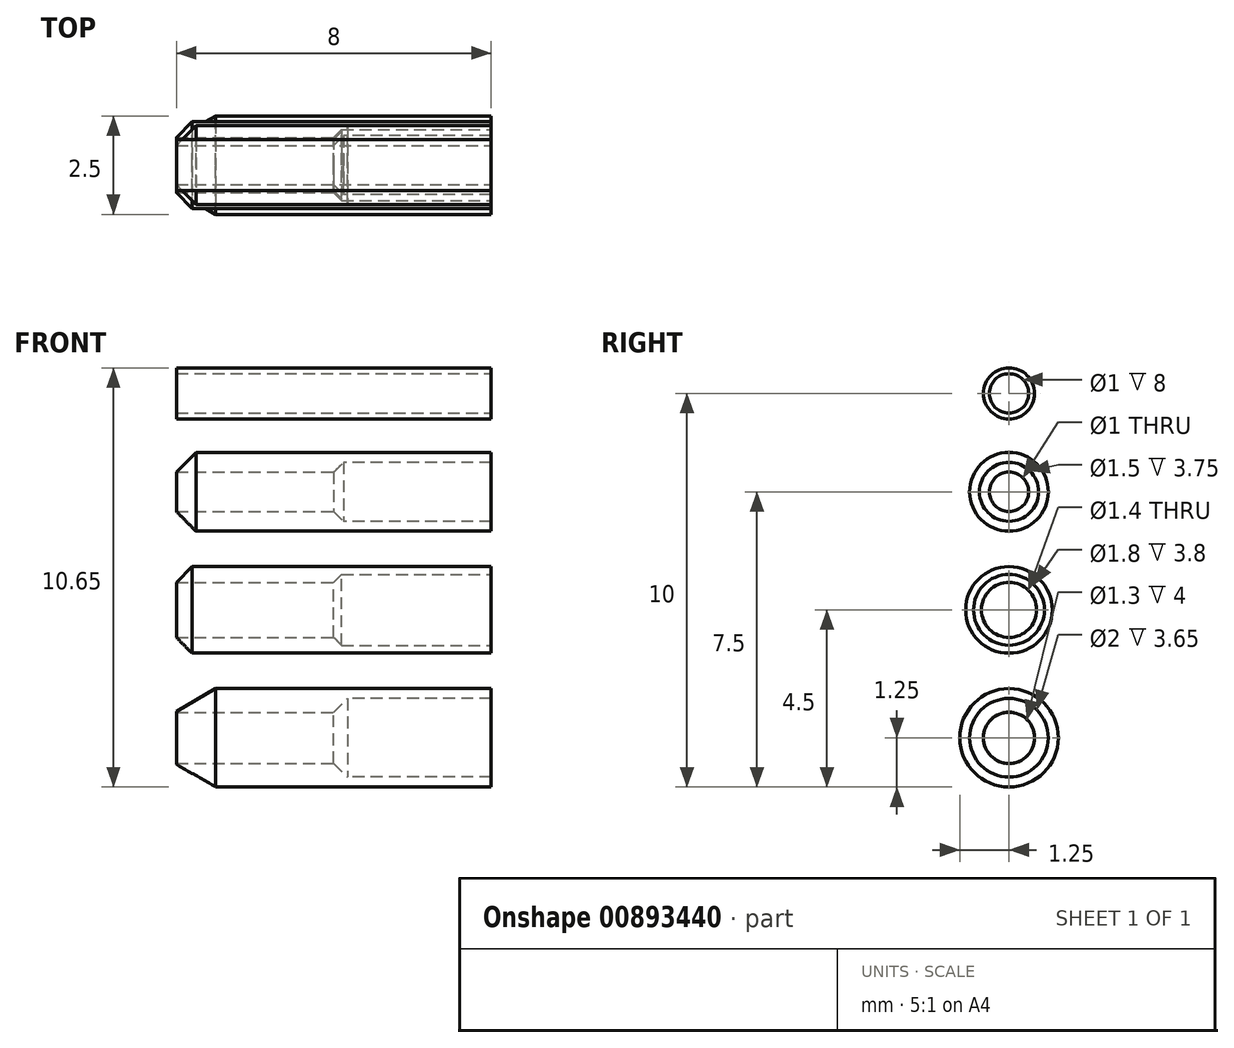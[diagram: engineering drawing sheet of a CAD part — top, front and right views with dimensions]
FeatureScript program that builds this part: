
annotation { "Feature Type Name" : "Feature", "Feature Type Description" : "" }
export const myFeature = defineFeature(function(context is Context, id is Id, definition is map)
    precondition{}
    {
        {
            var Q0;
            Q0=qCreatedBy(makeId("Right.planeOp"),FACE);
            var sketch = newSketch(context, id + "F0", { "sketchPlane" : qUnion([Q0])});
            skCircle(sketch, "E0", {"center": v(0, 0) * mm, "radius": 1.1 * mm});
            skCircle(sketch, "E1", {"center": v(0, 3) * mm, "radius": 1 * mm});
            skCircle(sketch, "E2", {"center": v(0, -3.25) * mm, "radius": 1.25 * mm});
            skCircle(sketch, "E3", {"center": v(0, 5.5) * mm, "radius": 0.65 * mm});
            skSolve(sketch);
        }
        {
            var Q0;
            Q0 = qSketchRegion(id + "F0", true);
            extrude(context, id + "F1", {"entities" : qUnion([Q0]), "endBound" : BoundingType.SYMMETRIC, "depth" : 8 * mm, "offsetDistance" : 25 * mm});
        }
        {
            var Q0;
            Q0=makeQuery(id+"F1.opExtrude","CAP_FACE",FACE,{"disambiguationData":[OSD([sQuery(id+"F0.wireOp",EDGE,"E1")])],"isStart":false});
            var sketch = newSketch(context, id + "F2", { "sketchPlane" : qUnion([Q0])});
            skPoint(sketch, "E4", {"position": v(0, 0) * mm});
            skPoint(sketch, "E5", {"position": v(0, 3) * mm});
            skPoint(sketch, "E6", {"position": v(0, 5.5) * mm});
            skPoint(sketch, "E7", {"position": v(0, -3.25) * mm});
            skSolve(sketch);
        }
        {
            var Q0;
            Q0=sQuery(id+"F2.wireOp",VERTEX,"E6");
            var Q1;
            Q1=makeQuery(id+"F1.opExtrude","SWEPT_BODY",BODY,{"disambiguationData":[OSD([sQuery(id+"F0.wireOp",EDGE,"E3")])]});
            hole(context, id + "F3", {"style" : HoleStyle.SIMPLE, "endStyle" : HoleEndStyle.THROUGH, "holeDiameter" : 1 * mm, "majorDiameter" : 5 * mm, "isTappedThrough" : true, "tappedDepth" : 12 * mm, "tapClearance" : 3, "locations" : qUnion([Q0]), "scope" : qUnion([Q1])});
        }
        {
            var Q0;
            Q0=sQuery(id+"F2.wireOp",VERTEX,"E7");
            var Q1;
            Q1=makeQuery(id+"F1.opExtrude","SWEPT_BODY",BODY,{"disambiguationData":[OSD([sQuery(id+"F0.wireOp",EDGE,"E2")])]});
            hole(context, id + "F4", {"style" : HoleStyle.SIMPLE, "endStyle" : HoleEndStyle.THROUGH, "holeDiameter" : 1.3 * mm, "majorDiameter" : 5 * mm, "isTappedThrough" : true, "tappedDepth" : 12 * mm, "tapClearance" : 3, "locations" : qUnion([Q0]), "scope" : qUnion([Q1])});
        }
        {
            var Q0;
            Q0=sQuery(id+"F2.wireOp",VERTEX,"E4");
            var Q1;
            Q1=makeQuery(id+"F1.opExtrude","SWEPT_BODY",BODY,{"disambiguationData":[OSD([sQuery(id+"F0.wireOp",EDGE,"E0")])]});
            hole(context, id + "F5", {"style" : HoleStyle.SIMPLE, "endStyle" : HoleEndStyle.THROUGH, "holeDiameter" : 1.4 * mm, "majorDiameter" : 5 * mm, "isTappedThrough" : true, "tappedDepth" : 12 * mm, "tapClearance" : 3, "locations" : qUnion([Q0]), "scope" : qUnion([Q1])});
        }
        {
            var Q0;
            Q0=sQuery(id+"F2.wireOp",VERTEX,"E5");
            var Q1;
            Q1=makeQuery(id+"F1.opExtrude","SWEPT_BODY",BODY,{"disambiguationData":[OSD([sQuery(id+"F0.wireOp",EDGE,"E1")])]});
            hole(context, id + "F6", {"style" : HoleStyle.SIMPLE, "endStyle" : HoleEndStyle.THROUGH, "holeDiameter" : 1 * mm, "majorDiameter" : 5 * mm, "isTappedThrough" : true, "tappedDepth" : 12 * mm, "tapClearance" : 3, "locations" : qUnion([Q0]), "scope" : qUnion([Q1])});
        }
        {
            var Q0;
            Q0=makeQuery(id+"F1.opExtrude","CAP_EDGE",EDGE,{"disambiguationData":[OSD([sQuery(id+"F0.wireOp",EDGE,"E0")])],"isStart":true});
            chamfer(context, id + "F7", {"entities" : qUnion([Q0]), "chamferType" : ChamferType.OFFSET_ANGLE, "width" : .4 * mm, "oppositeDirection" : false, "angle" : 45 * degree, "tangentPropagation" : true});
        }
        {
            var Q0;
            Q0=makeQuery(id+"F1.opExtrude","CAP_EDGE",EDGE,{"disambiguationData":[OSD([sQuery(id+"F0.wireOp",EDGE,"E1")])],"isStart":true});
            chamfer(context, id + "F8", {"entities" : qUnion([Q0]), "chamferType" : ChamferType.OFFSET_ANGLE, "width" : 0.5 * mm, "oppositeDirection" : false, "angle" : 45 * degree, "tangentPropagation" : true});
        }
        {
            var Q0;
            Q0=makeQuery(id+"F1.opExtrude","CAP_EDGE",EDGE,{"disambiguationData":[OSD([sQuery(id+"F0.wireOp",EDGE,"E2")])],"isStart":true});
            chamfer(context, id + "F9", {"entities" : qUnion([Q0]), "chamferType" : ChamferType.OFFSET_ANGLE, "width" : 1 * mm, "oppositeDirection" : false, "angle" : 30 * degree, "tangentPropagation" : true});
        }
        {
            var Q0;
            Q0=qCreatedBy(makeId("Front.planeOp"),FACE);
            var sketch = newSketch(context, id + "F10", { "sketchPlane" : qUnion([Q0])});
            skLineSegment(sketch, "E8", {"start": v(4, -2.25) * mm, "end": v(0.35, -2.25) * mm});
            skLineSegment(sketch, "E9", {"start": v(0.35, -2.25) * mm, "end": v(0, -2.6) * mm});
            skLineSegment(sketch, "E10", {"start": v(0, -2.6) * mm, "end": v(0, -3.25) * mm});
            skLineSegment(sketch, "E11", {"start": v(4, -3.25) * mm, "end": v(0, -3.25) * mm});
            skLineSegment(sketch, "E12", {"start": v(4, -3.25) * mm, "end": v(4, -2.25) * mm});
            skSolve(sketch);
        }
        {
            var Q0;
            Q0 = qSketchRegion(id + "F10", true);
            var Q1;
            Q1=sQuery(id+"F10.wireOp",EDGE,"E11");
            revolve(context, id + "F11", {"operationType" : NewBodyOperationType.REMOVE, "surfaceOperationType" : NewSurfaceOperationType.NEW, "entities" : qUnion([Q0]), "axis" : qUnion([Q1]), "revolveType" : RevolveType.FULL, "oppositeDirection" : true});
        }
        {
            var Q0;
            Q0=qCreatedBy(makeId("Front.planeOp"),FACE);
            var sketch = newSketch(context, id + "F12", { "sketchPlane" : qUnion([Q0])});
            skLineSegment(sketch, "E13", {"start": v(0, 0) * mm, "end": v(4, 0) * mm});
            skLineSegment(sketch, "E14", {"start": v(4, 0) * mm, "end": v(4, 0.9) * mm});
            skLineSegment(sketch, "E15", {"start": v(4, 0.9) * mm, "end": v(0.2, 0.9) * mm});
            skLineSegment(sketch, "E16", {"start": v(0.2, 0.9) * mm, "end": v(0, 0.7) * mm});
            skLineSegment(sketch, "E17", {"start": v(0, 0.7) * mm, "end": v(0, 0) * mm});
            skSolve(sketch);
        }
        {
            var Q0;
            Q0 = qSketchRegion(id + "F12", true);
            var Q1;
            Q1=sQuery(id+"F12.wireOp",EDGE,"E13");
            revolve(context, id + "F13", {"operationType" : NewBodyOperationType.REMOVE, "surfaceOperationType" : NewSurfaceOperationType.NEW, "entities" : qUnion([Q0]), "axis" : qUnion([Q1]), "revolveType" : RevolveType.FULL, "oppositeDirection" : true});
        }
        {
            var Q0;
            Q0=qCreatedBy(makeId("Front.planeOp"),FACE);
            var sketch = newSketch(context, id + "F14", { "sketchPlane" : qUnion([Q0])});
            skLineSegment(sketch, "E18", {"start": v(4, 3) * mm, "end": v(0, 3) * mm});
            skLineSegment(sketch, "E19", {"start": v(0, 3) * mm, "end": v(0, 3.5) * mm});
            skLineSegment(sketch, "E20", {"start": v(0, 3.5) * mm, "end": v(0.25, 3.75) * mm});
            skLineSegment(sketch, "E21", {"start": v(0.25, 3.75) * mm, "end": v(4, 3.75) * mm});
            skLineSegment(sketch, "E22", {"start": v(4, 3.75) * mm, "end": v(4, 3) * mm});
            skSolve(sketch);
        }
        {
            var Q0;
            Q0=makeQuery(id+"F14.imprint","IMPRINT",FACE,{"disambiguationData":[TD([[makeQuery(id+"F14.imprint","IMPRINT",EDGE,{"derivedFrom":sQuery(id+"F14.wireOp",EDGE,"E18")}),-1.0]])]});
            var Q1;
            Q1=sQuery(id+"F14.wireOp",EDGE,"E18");
            revolve(context, id + "F15", {"operationType" : NewBodyOperationType.REMOVE, "surfaceOperationType" : NewSurfaceOperationType.NEW, "entities" : qUnion([Q0]), "axis" : qUnion([Q1]), "revolveType" : RevolveType.FULL, "oppositeDirection" : true});
        }
    });
